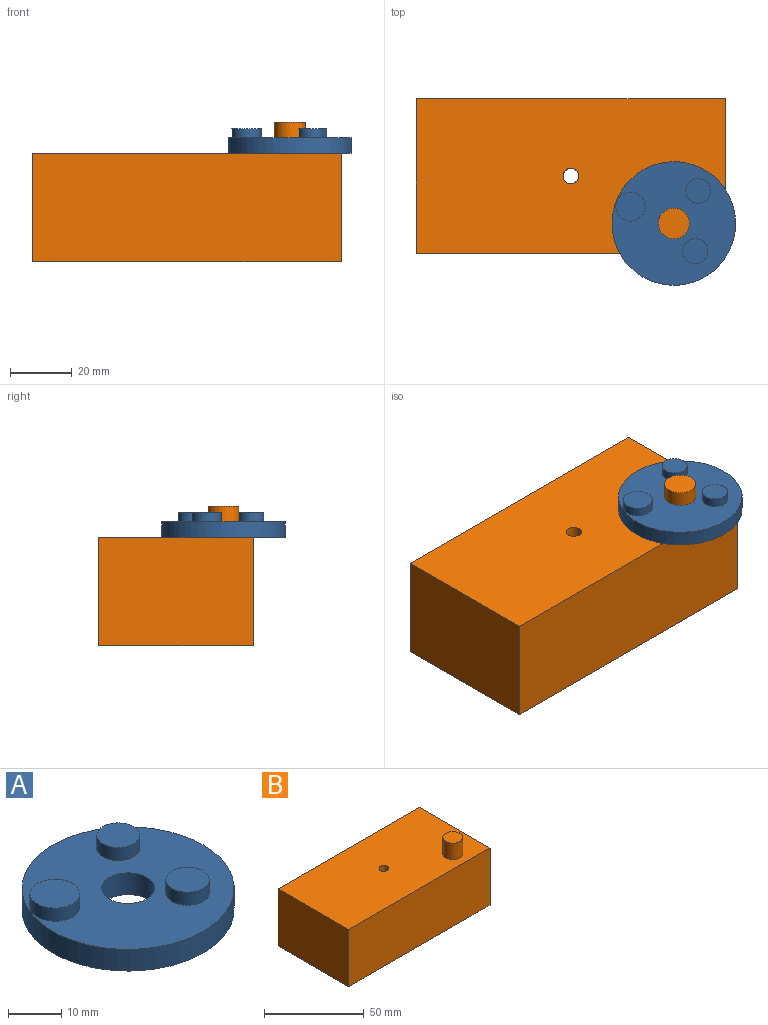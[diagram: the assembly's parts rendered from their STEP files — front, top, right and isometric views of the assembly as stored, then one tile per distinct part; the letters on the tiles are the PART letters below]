
ASSEMBLY  parts=2 mates=1
PART A: 10 faces, bbox 40x40x8 mm
  f0: cylinder r=5mm len=10mm, axis (0,0,-1), area 157.1mm2, adj f2,f3
  f1: cylinder r=20mm len=40mm, axis (0,0,-1), area 628.3mm2, adj f2,f3
  f2: plane 40x40mm, normal (0,0,1), area 1004.8mm2, adj f0,f1,f4,f6,f8
  f3: plane 40x40mm, normal (0,0,-1), area 1178.1mm2, adj f0,f1
  f4: cylinder r=4.04mm len=8.09mm, axis (0,0,-1), area 76.2mm2, adj f2,f5
  f5: plane 8.09x8.09mm, normal (0,0,1), area 51.4mm2, adj f4
  f6: cylinder r=4.08mm len=8.17mm, axis (0,0,-1), area 77mm2, adj f2,f7
  f7: plane 8.17x8.17mm, normal (0,0,1), area 52.4mm2, adj f6
  f8: cylinder r=4.71mm len=9.41mm, axis (0,0,-1), area 88.7mm2, adj f2,f9
  f9: plane 9.41x9.41mm, normal (0,0,1), area 69.5mm2, adj f8
PART B: 9 faces, bbox 100x50x45 mm
  f0: plane 100x35mm, normal (0,1,0), area 3500mm2, adj f1,f4,f5,f6
  f1: plane 50x35mm, normal (-1,0,0), area 1750mm2, adj f0,f2,f5,f6
  f2: plane 100x35mm, normal (0,-1,0), area 3500mm2, adj f1,f4,f5,f6
  f3: cylinder r=2.5mm len=35mm, axis (0,0,-1), area 549.8mm2, adj f5,f6
  f4: plane 50x35mm, normal (1,0,0), area 1750mm2, adj f0,f2,f5,f6
  f5: plane 100x50mm, normal (0,0,-1), area 4980.4mm2, adj f0,f1,f2,f3,f4
  f6: plane 100x50mm, normal (0,0,1), area 4901.8mm2, adj f0,f1,f2,f3,f4,f7
  f7: cylinder r=5mm len=10mm, axis (0,0,-1), area 314.2mm2, adj f6,f8
  f8: plane 10x10mm, normal (0,0,1), area 78.5mm2, adj f7
PLACE A t=(15.82,-15.77,47.09)mm
PLACE B t=(-17.53,-0.39,12.09)mm fixed
MATE revolute B.f7 <-> A.f0  axis (0,0,1) through (15.82,-15.77,47.09)mm
